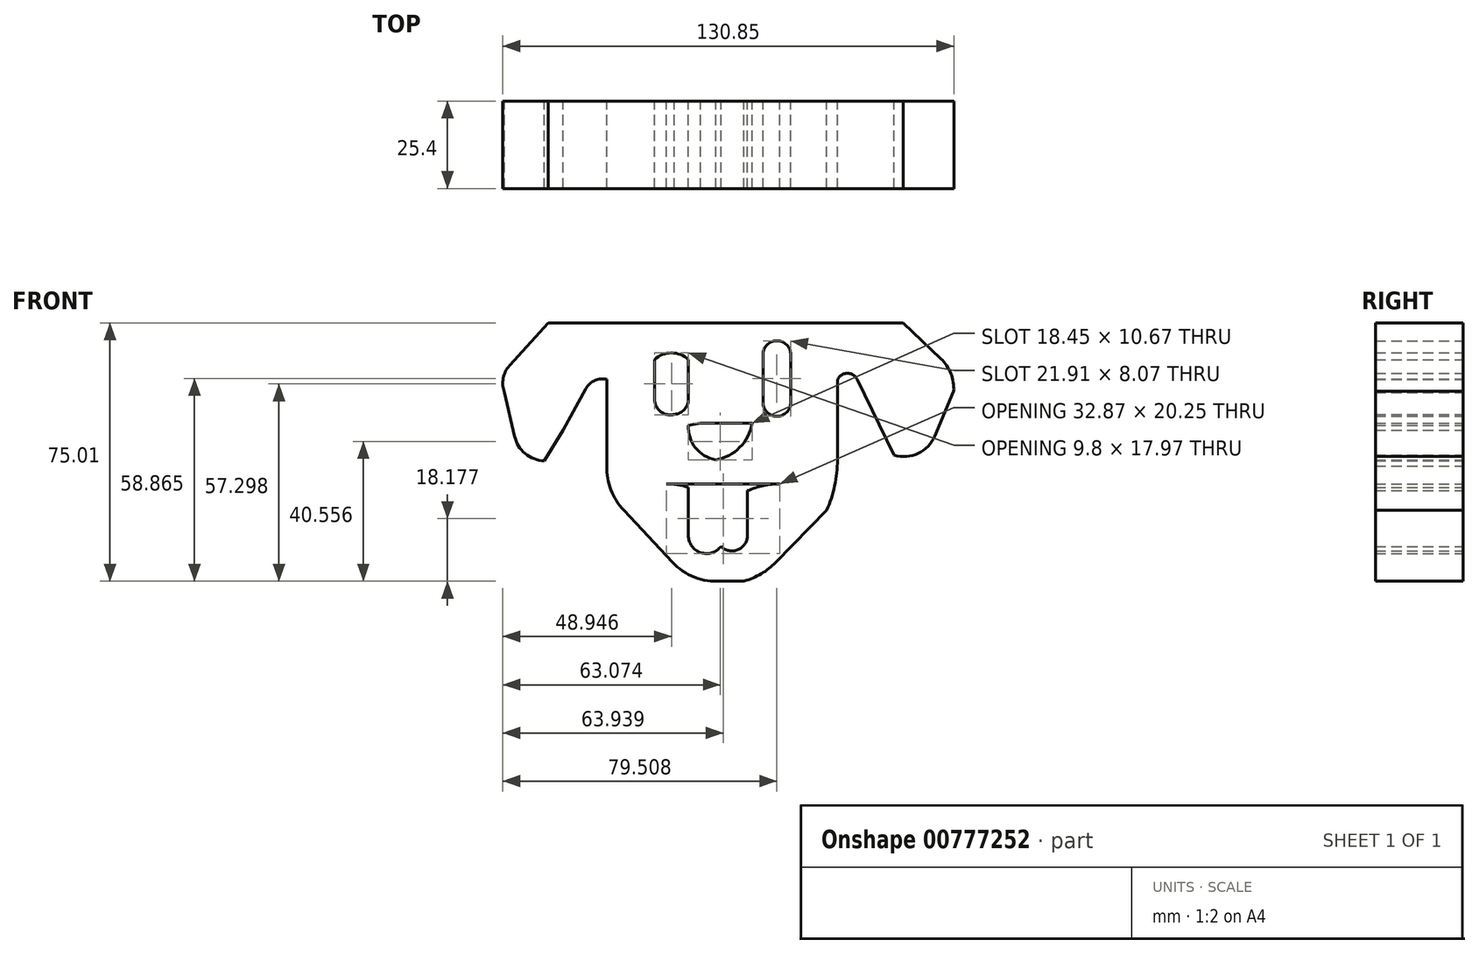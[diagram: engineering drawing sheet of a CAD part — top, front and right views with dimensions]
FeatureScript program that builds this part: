
annotation { "Feature Type Name" : "Feature", "Feature Type Description" : "" }
export const myFeature = defineFeature(function(context is Context, id is Id, definition is map)
    precondition{}
    {
        {
            var Q0;
            Q0=qCreatedBy(makeId("Front.planeOp"),FACE);
            var sketch = newSketch(context, id + "F0", { "sketchPlane" : qUnion([Q0])});
            skLineSegment(sketch, "E0", {"start": v(-33.09, 37.99) * mm, "end": v(-33.09, 12.9) * mm});
            skLineSegment(sketch, "E1", {"start": v(-50.1, 54.42) * mm, "end": v(-61.34, 42.02) * mm});
            skLineSegment(sketch, "E2", {"start": v(-59.9, 21.55) * mm, "end": v(-62.78, 34.24) * mm});
            skArc(sketch, "E3", {"start": v(-61.34, 42.02) * mm, "mid": v(-63.17, 38.34) * mm, "end": v(-62.78, 34.24) * mm});
            skLineSegment(sketch, "E4", {"start": v(-51.25, 14.34) * mm, "end": v(-45.77, 23.28) * mm});
            skArc(sketch, "E5", {"start": v(-59.9, 21.55) * mm, "mid": v(-56.8, 16.48) * mm, "end": v(-51.25, 14.34) * mm});
            skLineSegment(sketch, "E6", {"start": v(-45.77, 23.28) * mm, "end": v(-39.14, 35.4) * mm});
            skArc(sketch, "E7", {"start": v(-33.09, 37.99) * mm, "mid": v(-36.56, 37.73) * mm, "end": v(-39.14, 35.4) * mm});
            skLineSegment(sketch, "E8", {"start": v(-50.1, 54.42) * mm, "end": v(5.26, 54.42) * mm});
            skLineSegment(sketch, "E9", {"start": v(5.26, 54.42) * mm, "end": v(22.85, 54.42) * mm});
            skLineSegment(sketch, "E10", {"start": v(-28.18, 0) * mm, "end": v(-14.06, -15.06) * mm});
            skArc(sketch, "E11", {"start": v(-33.09, 12.9) * mm, "mid": v(-31.9, 5.97) * mm, "end": v(-28.18, 0) * mm});
            skLineSegment(sketch, "E12", {"start": v(0, -20.54) * mm, "end": v(6.7, -20.54) * mm});
            skArc(sketch, "E13", {"start": v(-14.06, -15.06) * mm, "mid": v(-7.65, -19.4) * mm, "end": v(0, -20.54) * mm});
            skLineSegment(sketch, "E14", {"start": v(15.93, -15.06) * mm, "end": v(30.63, 0) * mm});
            skArc(sketch, "E15", {"start": v(6.7, -20.54) * mm, "mid": v(11.68, -18.41) * mm, "end": v(15.93, -15.06) * mm});
            skLineSegment(sketch, "E16", {"start": v(33.8, 37.99) * mm, "end": v(33.8, 14.63) * mm});
            skArc(sketch, "E17", {"start": v(30.63, 0) * mm, "mid": v(33, 7.15) * mm, "end": v(33.8, 14.63) * mm});
            skLineSegment(sketch, "E18", {"start": v(39.57, 37.99) * mm, "end": v(50.24, 16.07) * mm});
            skArc(sketch, "E19", {"start": v(39.57, 37.99) * mm, "mid": v(36.69, 39.79) * mm, "end": v(33.8, 37.99) * mm});
            skLineSegment(sketch, "E20", {"start": v(67.54, 34.53) * mm, "end": v(62.06, 21.55) * mm});
            skArc(sketch, "E21", {"start": v(50.24, 16.07) * mm, "mid": v(57.2, 16.53) * mm, "end": v(62.06, 21.55) * mm});
            skLineSegment(sketch, "E22", {"start": v(52.84, 54.42) * mm, "end": v(63.8, 44.04) * mm});
            skLineSegment(sketch, "E23", {"start": v(52.84, 54.42) * mm, "end": v(25.16, 54.42) * mm});
            skLineSegment(sketch, "E24", {"start": v(25.16, 54.42) * mm, "end": v(22.85, 54.42) * mm});
            skArc(sketch, "E25", {"start": v(67.54, 34.53) * mm, "mid": v(66.72, 39.7) * mm, "end": v(63.8, 44.04) * mm});
            skLineSegment(sketch, "E26", {"start": v(-5.98, 25.3) * mm, "end": v(9.01, 25.3) * mm});
            skArc(sketch, "E27", {"start": v(-1.53, 14.63) * mm, "mid": v(5.45, 18.28) * mm, "end": v(9.01, 25.3) * mm});
            skArc(sketch, "E28", {"start": v(-9.44, 24.72) * mm, "mid": v(-7.4, 18.18) * mm, "end": v(-1.53, 14.63) * mm});
            skLineSegment(sketch, "E29", {"start": v(-9.44, 24.72) * mm, "end": v(-5.98, 25.3) * mm});
            skLineSegment(sketch, "E30", {"start": v(-19.25, 43.75) * mm, "end": v(-19.25, 32.22) * mm});
            skLineSegment(sketch, "E31", {"start": v(-9.44, 43.75) * mm, "end": v(-9.45, 32.22) * mm});
            skArc(sketch, "E32", {"start": v(-13.48, 27.9) * mm, "mid": v(-10.62, 29.27) * mm, "end": v(-9.45, 32.22) * mm});
            skArc(sketch, "E33", {"start": v(-19.25, 32.22) * mm, "mid": v(-17.44, 28.62) * mm, "end": v(-13.48, 27.9) * mm});
            skArc(sketch, "E34", {"start": v(-9.44, 43.75) * mm, "mid": v(-14.34, 45.7) * mm, "end": v(-19.25, 43.75) * mm});
            skLineSegment(sketch, "E35", {"start": v(-9.45, 7.71) * mm, "end": v(17.08, 7.71) * mm});
            skLineSegment(sketch, "E36", {"start": v(-9.45, 7.71) * mm, "end": v(-15.79, 7.71) * mm});
            skArc(sketch, "E37", {"start": v(0, 0) * mm, "mid": v(-7, 5.68) * mm, "end": v(-15.79, 7.71) * mm});
            skArc(sketch, "E38", {"start": v(17.08, 7.71) * mm, "mid": v(7.71, 5.7) * mm, "end": v(0, 0) * mm});
            skLineSegment(sketch, "E39", {"start": v(-9.45, 7.71) * mm, "end": v(-9.45, -7.28) * mm});
            skLineSegment(sketch, "E40", {"start": v(7.71, 5.7) * mm, "end": v(7.71, -7.28) * mm});
            skArc(sketch, "E41", {"start": v(0, -10.45) * mm, "mid": v(4.92, -11.45) * mm, "end": v(7.71, -7.28) * mm});
            skArc(sketch, "E42", {"start": v(-9.45, -7.28) * mm, "mid": v(-5.87, -12.27) * mm, "end": v(0, -10.45) * mm});
            skLineSegment(sketch, "E43", {"start": v(12.18, 45.2) * mm, "end": v(12.18, 31.36) * mm});
            skLineSegment(sketch, "E44", {"start": v(20.25, 45.2) * mm, "end": v(20.25, 31.36) * mm});
            skArc(sketch, "E45", {"start": v(20.25, 45.2) * mm, "mid": v(16.22, 49.23) * mm, "end": v(12.18, 45.2) * mm});
            skArc(sketch, "E46", {"start": v(12.18, 31.36) * mm, "mid": v(16.22, 27.32) * mm, "end": v(20.25, 31.36) * mm});
            skSolve(sketch);
        }
        {
            var Q0;
            Q0 = qSketchRegion(id + "F0", true);
            extrude(context, id + "F1", {"entities" : qUnion([Q0]), "depth" : 25.4 * mm, "offsetDistance" : 25.4 * mm});
        }
    });
